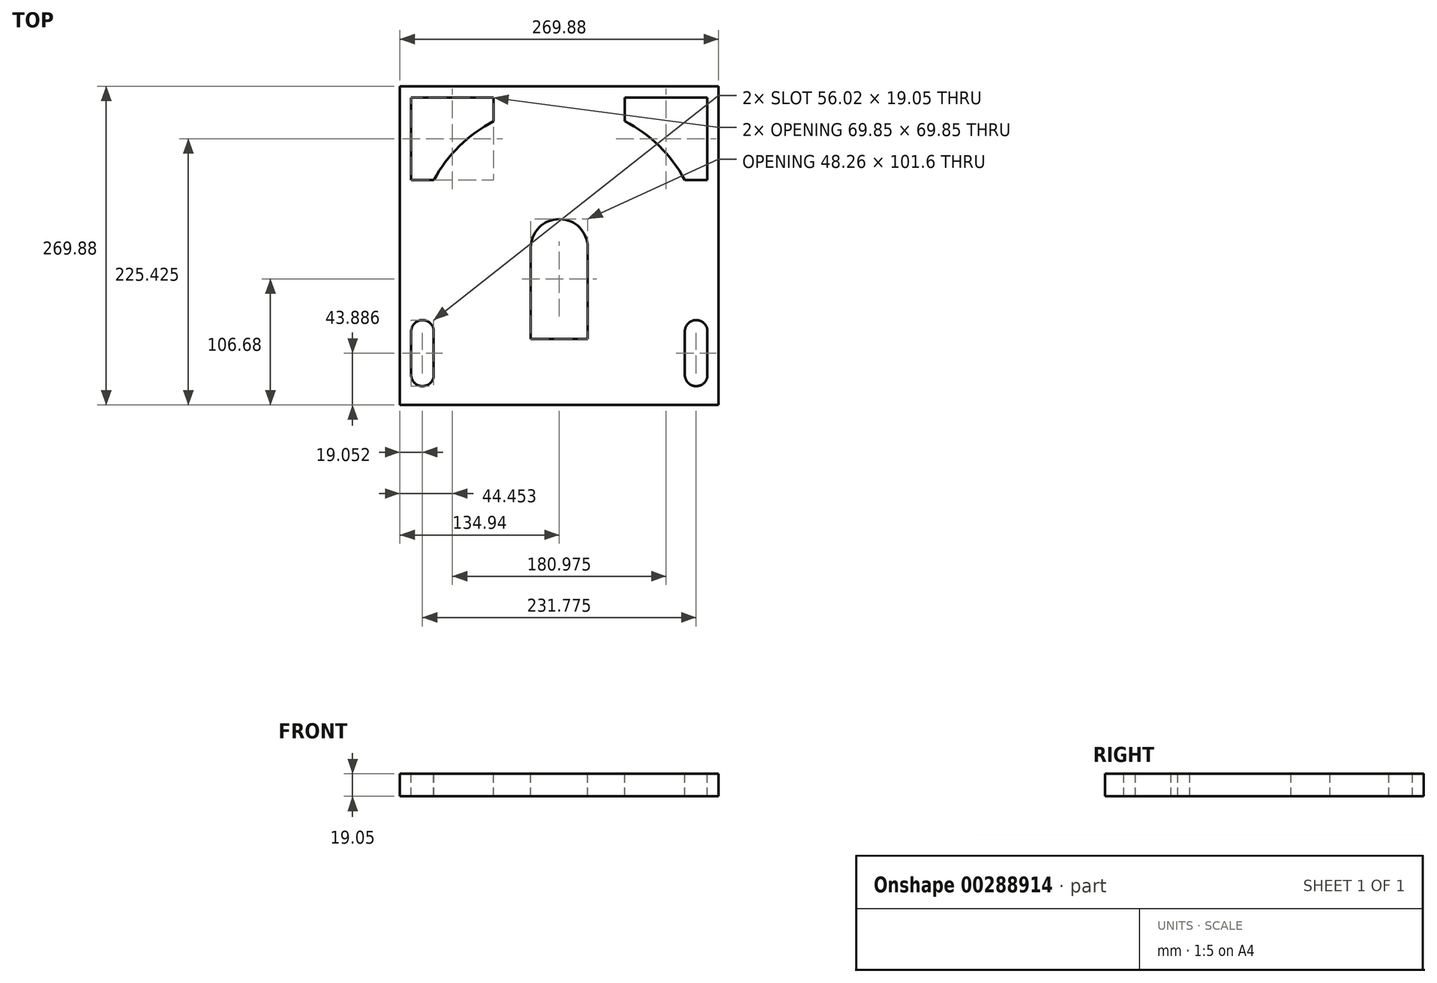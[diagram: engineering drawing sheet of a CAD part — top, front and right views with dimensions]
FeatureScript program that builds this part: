
annotation { "Feature Type Name" : "Feature", "Feature Type Description" : "" }
export const myFeature = defineFeature(function(context is Context, id is Id, definition is map)
    precondition{}
    {
        {
            var Q0;
            Q0=qCreatedBy(makeId("Top.planeOp"),FACE);
            var sketch = newSketch(context, id + "F0", { "sketchPlane" : qUnion([Q0])});
            skLineSegment(sketch, "E0.bottom", {"start": v(-134.94, 136.52) * mm, "end": v(134.94, 136.52) * mm});
            skLineSegment(sketch, "E0.top", {"start": v(-134.94, -136.53) * mm, "end": v(134.94, -136.53) * mm});
            skLineSegment(sketch, "E0.left", {"start": v(-134.94, 136.52) * mm, "end": v(-134.94, -136.53) * mm});
            skLineSegment(sketch, "E0.right", {"start": v(134.94, 136.52) * mm, "end": v(134.94, -136.53) * mm});
            skPoint(sketch, "E0.middle", {"position": v(0, 0) * mm});
            skSolve(sketch);
        }
        {
            var Q0;
            Q0 = qSketchRegion(id + "F0", true);
            extrude(context, id + "F1", {"entities" : qUnion([Q0]), "depth" : 19.05 * mm});
        }
        {
            var Q0;
            Q0=makeQuery(id+"F1.opExtrude","CAP_FACE",FACE,{"disambiguationData":[OSD([sQuery(id+"F0.wireOp",EDGE,"E0.bottom"),sQuery(id+"F0.wireOp",EDGE,"E0.top"),sQuery(id+"F0.wireOp",EDGE,"E0.left"),sQuery(id+"F0.wireOp",EDGE,"E0.right")])],"isStart":false});
            var sketch = newSketch(context, id + "F2", { "sketchPlane" : qUnion([Q0])});
            skLineSegment(sketch, "E1", {"start": v(-125.41, 136.52) * mm, "end": v(-125.41, -136.53) * mm, "construction": true});
            skLineSegment(sketch, "E2", {"start": v(125.41, 136.52) * mm, "end": v(125.41, -136.53) * mm, "construction": true});
            skLineSegment(sketch, "E3", {"start": v(-134.94, 127) * mm, "end": v(134.94, 127) * mm, "construction": true});
            skLineSegment(sketch, "E4", {"start": v(-134.94, -117.48) * mm, "end": v(134.94, -117.47) * mm, "construction": true});
            skArc(sketch, "E5", {"start": v(-55.56, 107.1) * mm, "mid": v(-84.68, 85.94) * mm, "end": v(-106.26, 57.15) * mm});
            skLineSegment(sketch, "E6", {"start": v(-125.41, 127) * mm, "end": v(-125.41, 57.15) * mm});
            skLineSegment(sketch, "E7", {"start": v(-125.41, 57.15) * mm, "end": v(-106.26, 57.15) * mm});
            skLineSegment(sketch, "E8", {"start": v(-125.41, 127) * mm, "end": v(-55.56, 127) * mm});
            skLineSegment(sketch, "E9", {"start": v(-55.56, 127) * mm, "end": v(-55.56, 107.1) * mm});
            skLineSegment(sketch, "E10", {"start": v(125.41, 127) * mm, "end": v(125.41, 57.15) * mm});
            skLineSegment(sketch, "E11", {"start": v(125.41, 57.15) * mm, "end": v(106.26, 57.15) * mm});
            skLineSegment(sketch, "E12", {"start": v(125.41, 127) * mm, "end": v(55.56, 127) * mm});
            skLineSegment(sketch, "E13", {"start": v(55.56, 127) * mm, "end": v(55.56, 107.09) * mm});
            skArc(sketch, "E14.trimOffspring", {"start": v(106.26, 57.15) * mm, "mid": v(84.67, 85.94) * mm, "end": v(55.56, 107.09) * mm});
            skSolve(sketch);
        }
        {
            var Q0;
            Q0 = qSketchRegion(id + "F2", true);
            extrude(context, id + "F3", {"entities" : qUnion([Q0]), "operationType" : NewBodyOperationType.REMOVE, "endBound" : BoundingType.UP_TO_NEXT, "oppositeDirection" : true, "depth" : 19.05 * mm});
        }
        {
            var Q0;
            Q0=makeQuery(id+"F1.opExtrude","CAP_FACE",FACE,{"disambiguationData":[OSD([sQuery(id+"F0.wireOp",EDGE,"E0.bottom"),sQuery(id+"F0.wireOp",EDGE,"E0.top"),sQuery(id+"F0.wireOp",EDGE,"E0.left"),sQuery(id+"F0.wireOp",EDGE,"E0.right")])],"isStart":false});
            var sketch = newSketch(context, id + "F4", { "sketchPlane" : qUnion([Q0])});
            skLineSegment(sketch, "E15", {"start": v(-125.41, 136.52) * mm, "end": v(-125.41, -108.43) * mm, "construction": true});
            skLineSegment(sketch, "E16", {"start": v(125.41, 136.52) * mm, "end": v(125.41, -136.53) * mm, "construction": true});
            skLineSegment(sketch, "E17", {"start": v(-106.36, 136.52) * mm, "end": v(-106.36, -136.53) * mm, "construction": true});
            skLineSegment(sketch, "E18", {"start": v(106.36, 136.52) * mm, "end": v(106.36, -136.53) * mm, "construction": true});
            skLineSegment(sketch, "E19", {"start": v(-134.94, -71) * mm, "end": v(-125.41, -71) * mm, "construction": true});
            skLineSegment(sketch, "E20.left", {"start": v(-125.41, -108.43) * mm, "end": v(-125.41, -71) * mm});
            skLineSegment(sketch, "E20.right", {"start": v(-106.36, -117.48) * mm, "end": v(-106.36, -71) * mm});
            skLineSegment(sketch, "E21.top", {"start": v(106.36, -71) * mm, "end": v(125.41, -71) * mm});
            skLineSegment(sketch, "E21.left", {"start": v(106.36, -117.48) * mm, "end": v(106.36, -71) * mm});
            skLineSegment(sketch, "E21.right", {"start": v(125.41, -117.48) * mm, "end": v(125.41, -71) * mm});
            skArc(sketch, "E22", {"start": v(-106.36, -71.51) * mm, "mid": v(-115.89, -61.45) * mm, "end": v(-125.41, -71.51) * mm});
            skArc(sketch, "E23", {"start": v(-125.41, -107.45) * mm, "mid": v(-115.89, -117.48) * mm, "end": v(-106.36, -107.45) * mm});
            skLineSegment(sketch, "E24.trimOffspring", {"start": v(-125.41, -71) * mm, "end": v(-134.94, -71) * mm, "construction": true});
            skLineSegment(sketch, "E25.trimOffspring", {"start": v(-106.36, -71) * mm, "end": v(134.94, -71) * mm, "construction": true});
            skLineSegment(sketch, "E26.trimOffspring", {"start": v(-125.41, -117.48) * mm, "end": v(-125.41, -136.53) * mm, "construction": true});
            skLineSegment(sketch, "E27.trimOffspring", {"start": v(-106.36, -117.48) * mm, "end": v(106.36, -117.48) * mm, "construction": true});
            skPoint(sketch, "E28.orphan", {"position": v(-106.36, -107.94) * mm});
            skPoint(sketch, "E29.start.orphan", {"position": v(-125.41, -107.94) * mm});
            skLineSegment(sketch, "E30", {"start": v(-125.41, -71) * mm, "end": v(-125.41, -107.45) * mm});
            skLineSegment(sketch, "E31", {"start": v(-106.36, -71) * mm, "end": v(-106.36, -107.45) * mm});
            skLineSegment(sketch, "E32", {"start": v(-115.89, -107.94) * mm, "end": v(134.94, -107.94) * mm, "construction": true});
            skArc(sketch, "E33", {"start": v(125.41, -71.49) * mm, "mid": v(115.89, -61.46) * mm, "end": v(106.36, -71.49) * mm});
            skArc(sketch, "E34", {"start": v(106.36, -107.45) * mm, "mid": v(115.89, -117.48) * mm, "end": v(125.41, -107.45) * mm});
            skPoint(sketch, "E34.centerSnap0", {"position": v(115.89, -117.48) * mm});
            skLineSegment(sketch, "E35", {"start": v(106.36, -71) * mm, "end": v(106.36, -107.45) * mm});
            skLineSegment(sketch, "E36", {"start": v(125.41, -107.45) * mm, "end": v(125.41, -71.49) * mm});
            skLineSegment(sketch, "E37.trimOffspring", {"start": v(125.41, -117.48) * mm, "end": v(134.94, -117.48) * mm, "construction": true});
            skLineSegment(sketch, "E38", {"start": v(-115.89, -61.45) * mm, "end": v(115.89, -61.46) * mm, "construction": true});
            skSolve(sketch);
        }
        {
            var Q0;
            Q0 = qSketchRegion(id + "F4", true);
            extrude(context, id + "F5", {"entities" : qUnion([Q0]), "operationType" : NewBodyOperationType.REMOVE, "endBound" : BoundingType.UP_TO_NEXT, "oppositeDirection" : true, "depth" : 25.4 * mm});
        }
        {
            var Q0;
            Q0=makeQuery(id+"F1.opExtrude","CAP_FACE",FACE,{"disambiguationData":[OSD([sQuery(id+"F0.wireOp",EDGE,"E0.bottom"),sQuery(id+"F0.wireOp",EDGE,"E0.top"),sQuery(id+"F0.wireOp",EDGE,"E0.left"),sQuery(id+"F0.wireOp",EDGE,"E0.right")])],"isStart":false});
            var sketch = newSketch(context, id + "F6", { "sketchPlane" : qUnion([Q0])});
            skArc(sketch, "E39", {"start": v(24.13, 0) * mm, "mid": v(0, 24.13) * mm, "end": v(-24.13, 0) * mm});
            skLineSegment(sketch, "E40", {"start": v(-24.13, 0) * mm, "end": v(-24.13, -136.53) * mm, "construction": true});
            skLineSegment(sketch, "E41", {"start": v(24.13, 0) * mm, "end": v(24.13, -136.53) * mm, "construction": true});
            skLineSegment(sketch, "E42", {"start": v(0, 24.13) * mm, "end": v(-134.94, 24.13) * mm, "construction": true});
            skLineSegment(sketch, "E43", {"start": v(0, 24.13) * mm, "end": v(134.94, 24.13) * mm, "construction": true});
            skLineSegment(sketch, "E44", {"start": v(-134.94, -77.47) * mm, "end": v(134.94, -77.47) * mm, "construction": true});
            skLineSegment(sketch, "E45", {"start": v(-24.13, 0) * mm, "end": v(-24.13, -77.47) * mm});
            skLineSegment(sketch, "E46", {"start": v(-24.13, -77.47) * mm, "end": v(24.13, -77.47) * mm});
            skLineSegment(sketch, "E47", {"start": v(24.13, -77.47) * mm, "end": v(24.13, 0) * mm});
            skSolve(sketch);
        }
        {
            var Q0;
            Q0 = qSketchRegion(id + "F6", true);
            extrude(context, id + "F7", {"entities" : qUnion([Q0]), "operationType" : NewBodyOperationType.REMOVE, "endBound" : BoundingType.UP_TO_NEXT, "oppositeDirection" : true, "depth" : 3.17 * mm});
        }
        {
            var Q0;
            Q0=makeQuery(id+"F1.opExtrude","CAP_FACE",FACE,{"disambiguationData":[OSD([sQuery(id+"F0.wireOp",EDGE,"E0.bottom"),sQuery(id+"F0.wireOp",EDGE,"E0.top"),sQuery(id+"F0.wireOp",EDGE,"E0.left"),sQuery(id+"F0.wireOp",EDGE,"E0.right")])],"isStart":false});
            var sketch = newSketch(context, id + "F8", { "sketchPlane" : qUnion([Q0])});
            skLineSegment(sketch, "E48.bottom", {"start": v(-134.94, -136.53) * mm, "end": v(134.94, -136.53) * mm});
            skLineSegment(sketch, "E48.top", {"start": v(-134.94, -133.35) * mm, "end": v(134.94, -133.35) * mm});
            skLineSegment(sketch, "E48.left", {"start": v(-134.94, -136.53) * mm, "end": v(-134.94, -133.35) * mm});
            skLineSegment(sketch, "E48.right", {"start": v(134.94, -136.53) * mm, "end": v(134.94, -133.35) * mm});
            skSolve(sketch);
        }
        {
            var Q0;
            Q0 = qSketchRegion(id + "F8", true);
            extrude(context, id + "F9", {"entities" : qUnion([Q0]), "operationType" : NewBodyOperationType.REMOVE, "endBound" : BoundingType.UP_TO_NEXT, "oppositeDirection" : true, "depth" : 25.4 * mm});
        }
    });
